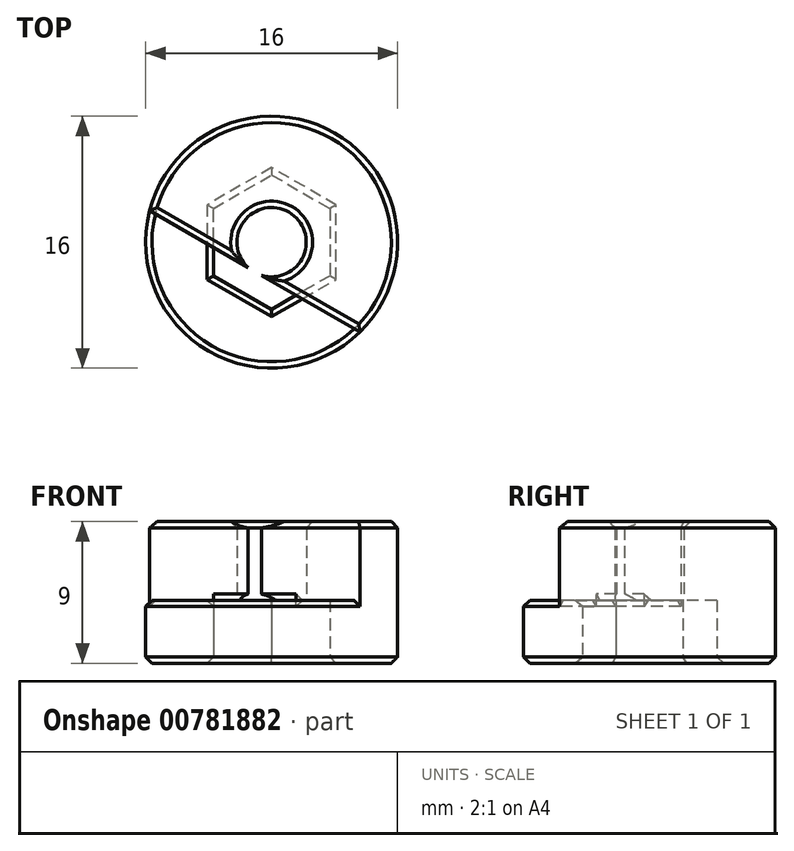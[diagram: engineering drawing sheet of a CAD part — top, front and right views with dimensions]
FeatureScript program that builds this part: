
annotation { "Feature Type Name" : "Feature", "Feature Type Description" : "" }
export const myFeature = defineFeature(function(context is Context, id is Id, definition is map)
    precondition{}
    {
        {
            var Q0;
            Q0=qCreatedBy(makeId("Top.planeOp"),FACE);
            var sketch = newSketch(context, id + "F0", { "sketchPlane" : qUnion([Q0])});
            skCircle(sketch, "E0.cCircle", {"center": v(0, 0) * mm, "radius": 3.7 * mm, "construction": true});
            skLineSegment(sketch, "E0.0", {"start": v(3.7, 2.14) * mm, "end": v(3.7, -2.14) * mm});
            skLineSegment(sketch, "E0.1", {"start": v(3.7, -2.14) * mm, "end": v(0, -4.27) * mm});
            skLineSegment(sketch, "E0.2", {"start": v(0, -4.27) * mm, "end": v(-3.7, -2.14) * mm});
            skLineSegment(sketch, "E0.3", {"start": v(-3.7, -2.14) * mm, "end": v(-3.7, 2.14) * mm});
            skLineSegment(sketch, "E0.4", {"start": v(-3.7, 2.14) * mm, "end": v(0, 4.27) * mm});
            skLineSegment(sketch, "E0.5", {"start": v(0, 4.27) * mm, "end": v(3.7, 2.14) * mm});
            skPoint(sketch, "E0.0.midPoint", {"position": v(3.7, 0) * mm});
            skCircle(sketch, "E1", {"center": v(0, 0) * mm, "radius": 8 * mm});
            skLineSegment(sketch, "E2", {"start": v(1.85, 3.2) * mm, "end": v(4, 6.93) * mm, "construction": true});
            skSolve(sketch);
        }
        {
            var Q0;
            Q0=qSketchRegion(id+"F0",true);
            extrude(context, id + "F1", {"entities" : qUnion([Q0]), "depth" : 4 * mm});
        }
        {
            var Q0;
            Q0=makeQuery(id+"F1.opExtrude","CAP_FACE",FACE,{"disambiguationData":[OSD([sQuery(id+"F0.wireOp",EDGE,"E0.0"),sQuery(id+"F0.wireOp",EDGE,"E0.1"),sQuery(id+"F0.wireOp",EDGE,"E0.2"),sQuery(id+"F0.wireOp",EDGE,"E0.3"),sQuery(id+"F0.wireOp",EDGE,"E0.4"),sQuery(id+"F0.wireOp",EDGE,"E0.5"),sQuery(id+"F0.wireOp",EDGE,"E1")])],"isStart":false});
            var sketch = newSketch(context, id + "F2", { "sketchPlane" : qUnion([Q0])});
            skArc(sketch, "E3", {"start": v(-0.64, -2.1) * mm, "mid": v(1.1, 1.9) * mm, "end": v(-1.5, -1.6) * mm});
            skArc(sketch, "E4", {"start": v(5.6, -5.7) * mm, "mid": v(4, 6.93) * mm, "end": v(-7.75, 2) * mm});
            skLineSegment(sketch, "E5", {"start": v(-7.75, 2) * mm, "end": v(-1.5, -1.6) * mm});
            skPoint(sketch, "E6", {"position": v(-1.5, -1.6) * mm});
            skPoint(sketch, "E7", {"position": v(-0.64, -2.1) * mm});
            skLineSegment(sketch, "E8.trimOffspring", {"start": v(-0.64, -2.1) * mm, "end": v(5.6, -5.7) * mm});
            skSolve(sketch);
        }
        {
            var Q0;
            Q0=qSketchRegion(id+"F2",true);
            extrude(context, id + "F3", {"entities" : qUnion([Q0]), "operationType" : NewBodyOperationType.ADD, "depth" : 5 * mm});
        }
        {
            var Q0;
            Q0=makeQuery(id+"F1.opExtrude","CAP_FACE",FACE,{"disambiguationData":[OSD([sQuery(id+"F0.wireOp",EDGE,"E0.0"),sQuery(id+"F0.wireOp",EDGE,"E0.1"),sQuery(id+"F0.wireOp",EDGE,"E0.2"),sQuery(id+"F0.wireOp",EDGE,"E0.3"),sQuery(id+"F0.wireOp",EDGE,"E0.4"),sQuery(id+"F0.wireOp",EDGE,"E0.5"),sQuery(id+"F0.wireOp",EDGE,"E1")])],"isStart":true});
            chamfer(context, id + "F4", {"entities" : qUnion([Q0]), "width" : 0.4 * mm, "tangentPropagation" : true});
        }
        {
            var Q0;
            Q0=makeQuery(id+"F3.opExtrude","CAP_FACE",FACE,{"disambiguationData":[OSD([sQuery(id+"F2.wireOp",EDGE,"E3"),sQuery(id+"F2.wireOp",EDGE,"E4"),sQuery(id+"F2.wireOp",EDGE,"E5"),sQuery(id+"F2.wireOp",EDGE,"E8.trimOffspring")])],"isStart":false});
            chamfer(context, id + "F5", {"entities" : qUnion([Q0]), "width" : 0.4 * mm, "tangentPropagation" : true});
        }
        {
            var Q0;
            {var subQ0=sQuery(id+"F0.wireOp",EDGE,"E0.3");var subQ2=sQuery(id+"F0.wireOp",EDGE,"E0.2");Q0=makeQuery(id+"F3.boolean.opBoolean","SPLIT",EDGE,{"disambiguationData":[TD([makeQuery(id+"F1.opExtrude","SWEPT_FACE",FACE,{"disambiguationData":[OSD([subQ2])]})])],"derivedFrom":makeQuery(id+"F1.opExtrude","CAP_EDGE",EDGE,{"disambiguationData":[OSD([subQ0])],"isStart":false})});}
            var Q1;
            Q1=makeQuery(id+"F1.opExtrude","CAP_EDGE",EDGE,{"disambiguationData":[OSD([sQuery(id+"F0.wireOp",EDGE,"E0.2")])],"isStart":false});
            var Q2;
            {var subQ0=sQuery(id+"F0.wireOp",EDGE,"E0.1");var subQ2=sQuery(id+"F0.wireOp",EDGE,"E0.2");Q2=makeQuery(id+"F3.boolean.opBoolean","SPLIT",EDGE,{"disambiguationData":[TD([makeQuery(id+"F1.opExtrude","SWEPT_FACE",FACE,{"disambiguationData":[OSD([subQ2])]})])],"derivedFrom":makeQuery(id+"F1.opExtrude","CAP_EDGE",EDGE,{"disambiguationData":[OSD([subQ0])],"isStart":false})});}
            var Q3;
            Q3=makeQuery(id+"F1.opExtrude","CAP_EDGE",EDGE,{"disambiguationData":[OSD([sQuery(id+"F0.wireOp",EDGE,"E1")])],"isStart":false});
            chamfer(context, id + "F6", {"entities" : qUnion([Q0, Q1, Q2, Q3]), "width" : 0.4 * mm, "tangentPropagation" : true});
        }
        {
            var Q0;
            {var subQ0=sQuery(id+"F2.wireOp",EDGE,"E5");var subQ2=sQuery(id+"F0.wireOp",EDGE,"E1");Q0=makeQuery(id+"F3.boolean.opBoolean","SPLIT",EDGE,{"disambiguationData":[TD([makeQuery(id+"F1.opExtrude","SWEPT_FACE",FACE,{"disambiguationData":[OSD([subQ2])]})])],"derivedFrom":makeQuery(id+"F3.opExtrude","CAP_EDGE",EDGE,{"disambiguationData":[OSD([subQ0])],"isStart":true})});}
            var Q1;
            {var subQ0=sQuery(id+"F2.wireOp",EDGE,"E8.trimOffspring");var subQ2=sQuery(id+"F0.wireOp",EDGE,"E1");Q1=makeQuery(id+"F3.boolean.opBoolean","SPLIT",EDGE,{"disambiguationData":[TD([makeQuery(id+"F1.opExtrude","SWEPT_FACE",FACE,{"disambiguationData":[OSD([subQ2])]})])],"derivedFrom":makeQuery(id+"F3.opExtrude","CAP_EDGE",EDGE,{"disambiguationData":[OSD([subQ0])],"isStart":true})});}
            chamfer(context, id + "F7", {"entities" : qUnion([Q0, Q1]), "width" : 0.4 * mm, "tangentPropagation" : true});
        }
    });
